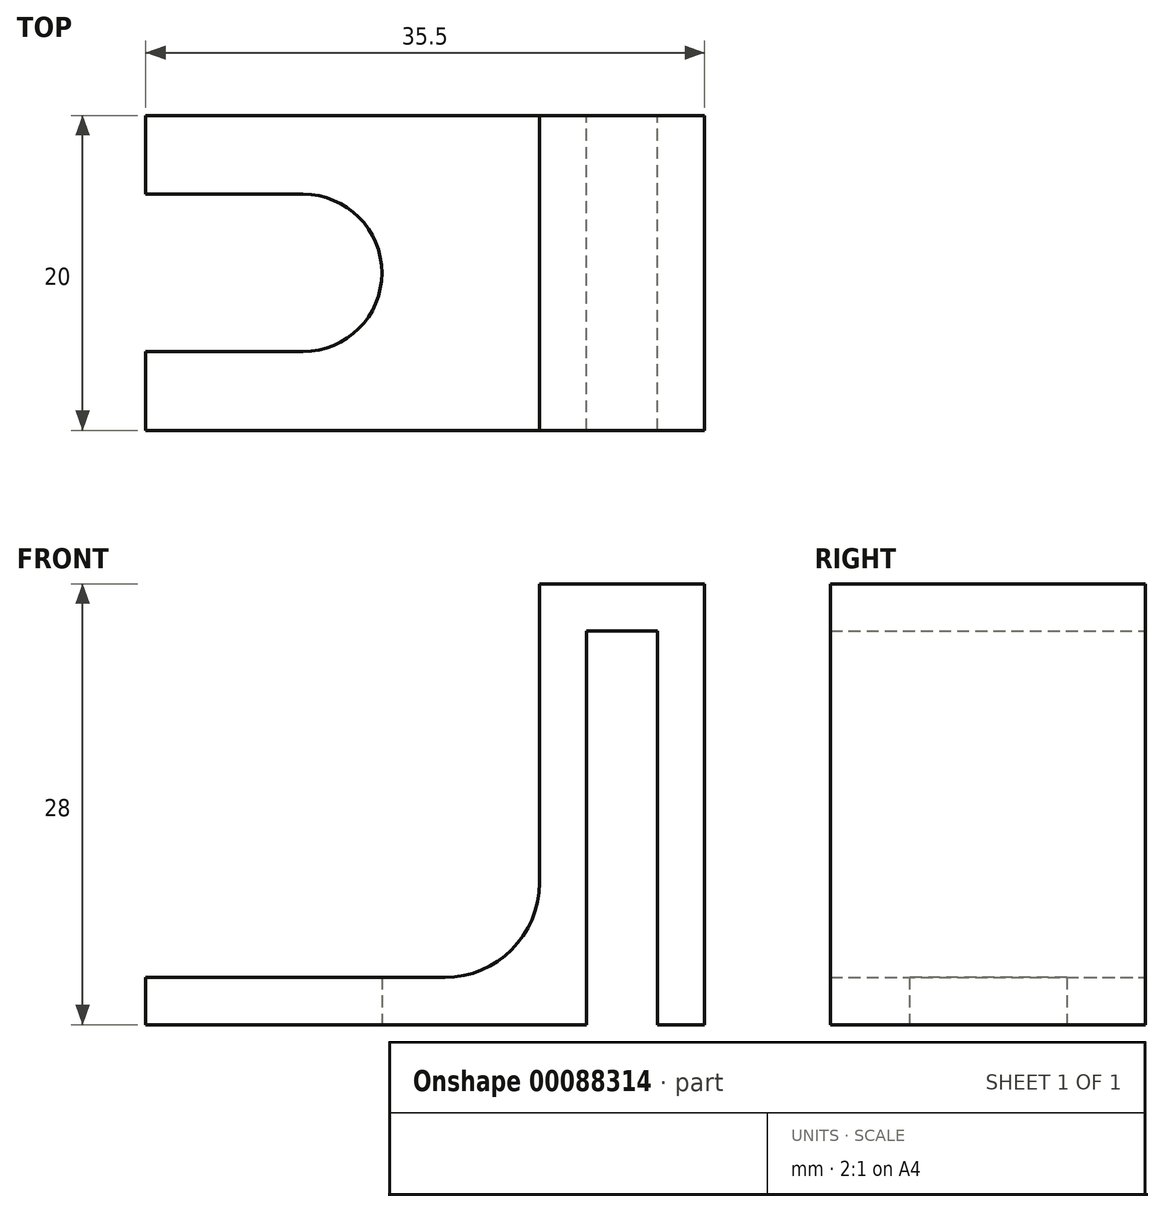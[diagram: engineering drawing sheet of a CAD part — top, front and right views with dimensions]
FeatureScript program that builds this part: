
annotation { "Feature Type Name" : "Feature", "Feature Type Description" : "" }
export const myFeature = defineFeature(function(context is Context, id is Id, definition is map)
    precondition{}
    {
        {
            var Q0;
            Q0=qCreatedBy(makeId("Front.planeOp"),FACE);
            var sketch = newSketch(context, id + "F0", { "sketchPlane" : qUnion([Q0])});
            skLineSegment(sketch, "E0.left", {"start": v(0, 0) * mm, "end": v(0, 3) * mm});
            skLineSegment(sketch, "E1.bottom", {"start": v(0, 0) * mm, "end": v(7.5, 0) * mm});
            skLineSegment(sketch, "E1.top", {"start": v(0, 3) * mm, "end": v(7.5, 3) * mm});
            skLineSegment(sketch, "E1.right", {"start": v(7.5, 0) * mm, "end": v(7.5, 3) * mm});
            skLineSegment(sketch, "E2.bottom", {"start": v(0, 3) * mm, "end": v(3, 3) * mm});
            skLineSegment(sketch, "E2.top", {"start": v(0, -25) * mm, "end": v(3, -25) * mm});
            skLineSegment(sketch, "E2.left", {"start": v(0, 3) * mm, "end": v(0, -25) * mm});
            skLineSegment(sketch, "E2.right", {"start": v(3, 3) * mm, "end": v(3, -25) * mm});
            skLineSegment(sketch, "E3.bottom", {"start": v(7.5, 3) * mm, "end": v(10.5, 3) * mm});
            skLineSegment(sketch, "E3.top", {"start": v(7.5, -25) * mm, "end": v(10.5, -25) * mm});
            skLineSegment(sketch, "E3.left", {"start": v(7.5, 3) * mm, "end": v(7.5, -25) * mm});
            skLineSegment(sketch, "E3.right", {"start": v(10.5, 3) * mm, "end": v(10.5, -25) * mm});
            skLineSegment(sketch, "E4.bottom", {"start": v(0, -25) * mm, "end": v(-25, -25) * mm});
            skLineSegment(sketch, "E4.top", {"start": v(0, -22) * mm, "end": v(-25, -22) * mm});
            skLineSegment(sketch, "E4.left", {"start": v(0, -25) * mm, "end": v(0, -22) * mm});
            skLineSegment(sketch, "E4.right", {"start": v(-25, -25) * mm, "end": v(-25, -22) * mm});
            skPoint(sketch, "E0.bottom.end.orphan", {"position": v(-25, 0) * mm});
            skSolve(sketch);
        }
        {
            var Q0;
            Q0 = qSketchRegion(id + "F0", true);
            extrude(context, id + "F1", {"entities" : qUnion([Q0]), "depth" : 10 * mm, "offsetDistance" : 25 * mm, "hasSecondDirection" : true, "secondDirectionOppositeDirection" : true, "secondDirectionDepth" : 10 * mm});
        }
        {
            var Q0;
            Q0=qCreatedBy(makeId("Top.planeOp"),FACE);
            cPlane(context, id + "F2", {"entities" : qUnion([Q0]), "cplaneType" : CPlaneType.OFFSET, "offset" : 20 * mm, "oppositeDirection" : true, "width" : 150 * mm, "height" : 150 * mm});
        }
        {
            var Q0;
            Q0=qCreatedBy(id+"F2.planeOp",FACE);
            var sketch = newSketch(context, id + "F3", { "sketchPlane" : qUnion([Q0])});
            skLineSegment(sketch, "E5.0.0", {"start": v(0, 10) * mm, "end": v(-25, 10) * mm, "construction": true});
            skLineSegment(sketch, "E5.0.1", {"start": v(-25, 10) * mm, "end": v(-25, 5) * mm, "construction": true});
            skLineSegment(sketch, "E5.0.2", {"start": v(-25, -10) * mm, "end": v(0, -10) * mm, "construction": true});
            skLineSegment(sketch, "E5.0.3", {"start": v(0, -10) * mm, "end": v(0, 10) * mm, "construction": true});
            skLineSegment(sketch, "E6.bottom", {"start": v(-10, 0) * mm, "end": v(-25, 0) * mm});
            skLineSegment(sketch, "E6.top", {"start": v(-15, 5) * mm, "end": v(-25, 5) * mm});
            skLineSegment(sketch, "E6.right", {"start": v(-25, 0) * mm, "end": v(-25, 5) * mm});
            skLineSegment(sketch, "E7.MirrorCS", {"start": v(-15, -5) * mm, "end": v(-25, -5) * mm});
            skArc(sketch, "E8", {"start": v(-15, -5) * mm, "mid": v(-10, 0) * mm, "end": v(-15, 5) * mm});
            skLineSegment(sketch, "E9.trimOffspring", {"start": v(-25, -5) * mm, "end": v(-25, -10) * mm, "construction": true});
            skPoint(sketch, "E10.orphan", {"position": v(-10, 5) * mm});
            skPoint(sketch, "E11.orphan", {"position": v(-10, -5) * mm});
            skLineSegment(sketch, "E12", {"start": v(-25, 5) * mm, "end": v(-25, -5) * mm});
            skSolve(sketch);
        }
        {
            var Q0;
            Q0 = qSketchRegion(id + "F3", true);
            extrude(context, id + "F4", {"entities" : qUnion([Q0]), "operationType" : NewBodyOperationType.REMOVE, "depth" : 10 * mm, "offsetDistance" : 25 * mm, "hasSecondDirection" : true, "secondDirectionOppositeDirection" : true, "secondDirectionDepth" : 10 * mm});
        }
        {
            var Q0;
            Q0=makeQuery(id+"F1.opExtrude","SWEPT_EDGE",EDGE,{"disambiguationData":[OSD([sQuery(id+"F0.wireOp",EDGE,"E2.left"),sQuery(id+"F0.wireOp",EDGE,"E4.top"),sQuery(id+"F0.wireOp",EDGE,"E4.left")])]});
            fillet(context, id + "F5", {"entities" : qUnion([Q0]), "radius" : 6 * mm, "tangentPropagation" : true, "allowEdgeOverflow" : false});
        }
    });
